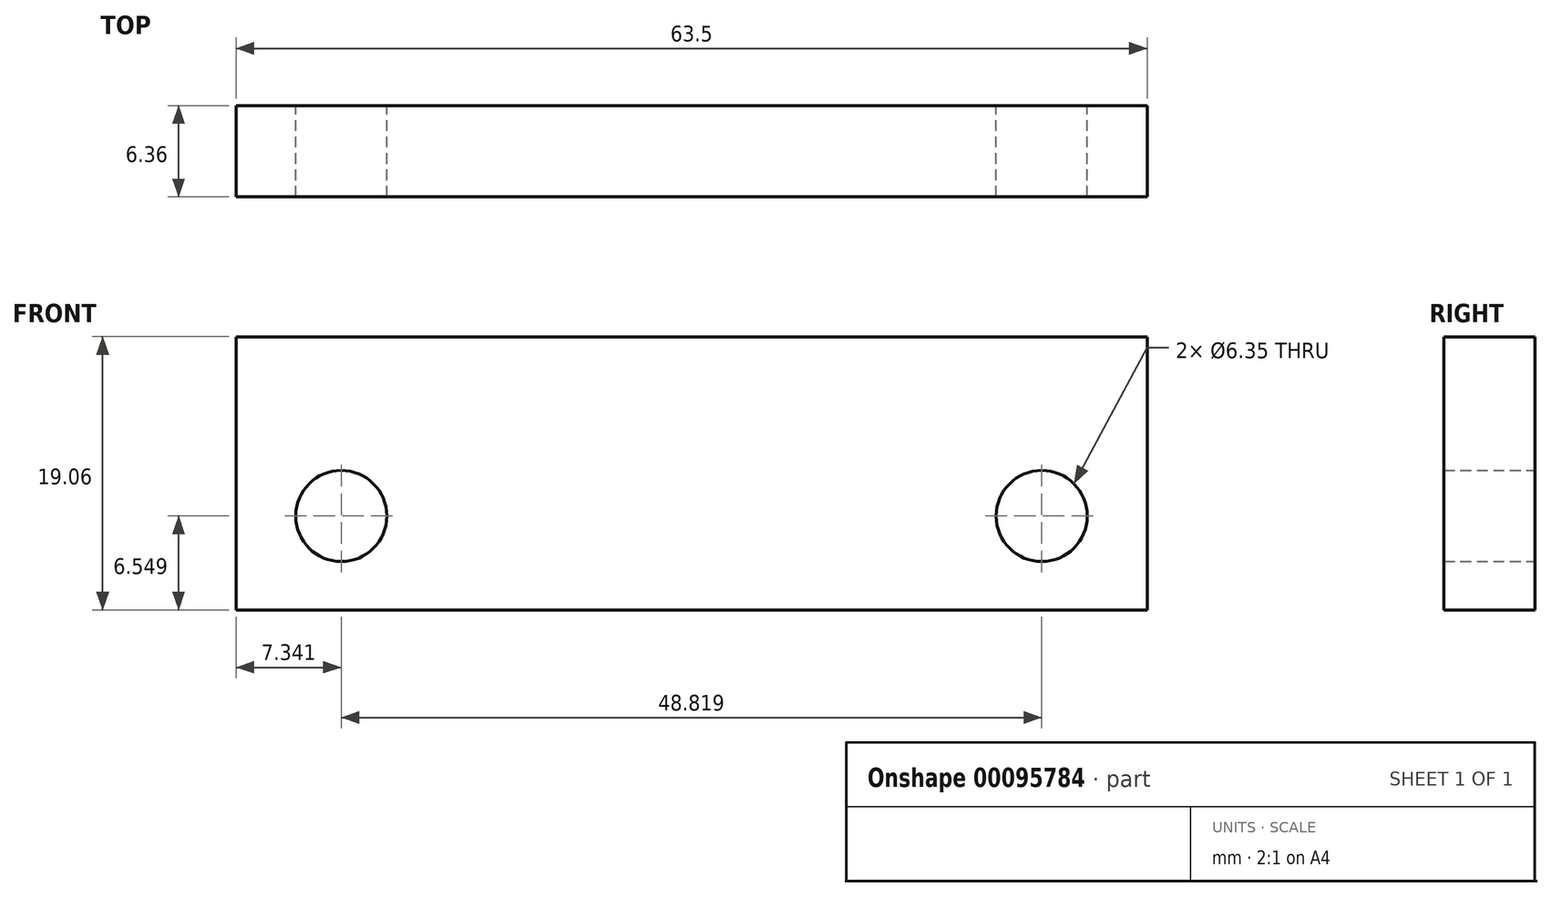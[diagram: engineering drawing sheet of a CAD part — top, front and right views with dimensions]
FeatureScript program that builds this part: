
annotation { "Feature Type Name" : "Feature", "Feature Type Description" : "" }
export const myFeature = defineFeature(function(context is Context, id is Id, definition is map)
    precondition{}
    {
        {
            var Q0;
            Q0=qCreatedBy(makeId("Front.planeOp"),FACE);
            var sketch = newSketch(context, id + "F0", { "sketchPlane" : qUnion([Q0])});
            skLineSegment(sketch, "E0.bottom", {"start": v(-31.75, 9.52) * mm, "end": v(31.75, 9.52) * mm});
            skLineSegment(sketch, "E0.top", {"start": v(-31.75, -9.53) * mm, "end": v(31.75, -9.53) * mm});
            skLineSegment(sketch, "E0.left", {"start": v(-31.75, 9.52) * mm, "end": v(-31.75, -9.53) * mm});
            skLineSegment(sketch, "E0.right", {"start": v(31.75, 9.52) * mm, "end": v(31.75, -9.52) * mm});
            skPoint(sketch, "E0.middle", {"position": v(0, 0) * mm});
            skCircle(sketch, "E1", {"center": v(-24.4, -2.98) * mm, "radius": 3.18 * mm});
            skCircle(sketch, "E2.MirrorC", {"center": v(24.4, -2.98) * mm, "radius": 3.18 * mm});
            skSolve(sketch);
        }
        {
            var Q0;
            Q0=makeQuery(id+"F0.imprint","IMPRINT",FACE,{"disambiguationData":[TD([[makeQuery(id+"F0.imprint","IMPRINT",EDGE,{"derivedFrom":sQuery(id+"F0.wireOp",EDGE,"E0.bottom")}),-1.0]])]});
            extrude(context, id + "F1", {"entities" : qUnion([Q0]), "endBound" : BoundingType.SYMMETRIC, "depth" : 6.35 * mm});
        }
    });
